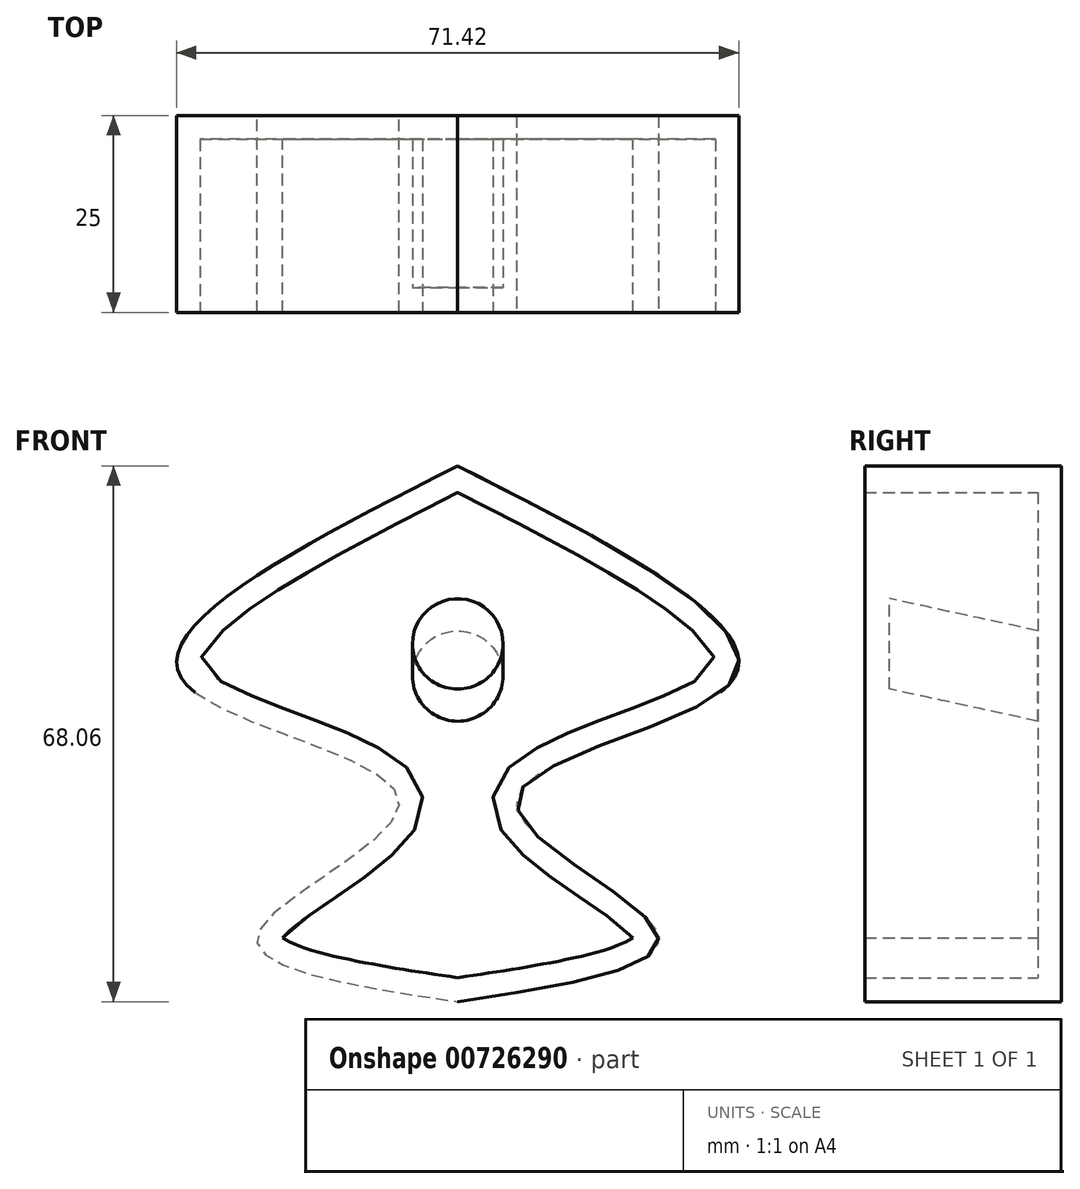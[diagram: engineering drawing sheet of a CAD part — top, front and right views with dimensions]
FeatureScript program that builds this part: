
annotation { "Feature Type Name" : "Feature", "Feature Type Description" : "" }
export const myFeature = defineFeature(function(context is Context, id is Id, definition is map)
    precondition{}
    {
        {
            var Q0;
            Q0=qCreatedBy(makeId("Front.planeOp"),FACE);
            var sketch = newSketch(context, id + "F0", { "sketchPlane" : qUnion([Q0])});
            skFitSpline(sketch, "E0", {"points": [v(0, 27.34) * mm, v(-34.86, 0) * mm, v(-7.47, -15.18) * mm, v(-25.3, -31.87) * mm, v(0, -40.72) * mm], "startDerivative": vector(-202.32, -102.92) * mm, "endDerivative": vector(177.56, -26.56) * mm});
            skFitSpline(sketch, "E1.MirrorCS", {"points": [v(0, 27.34) * mm, v(34.86, 0) * mm, v(7.47, -15.18) * mm, v(25.3, -31.87) * mm, v(0, -40.72) * mm], "startDerivative": vector(202.32, -102.92) * mm, "endDerivative": vector(-177.56, -26.56) * mm});
            skSolve(sketch);
        }
        {
            var Q0;
            Q0 = qSketchRegion(id + "F0", true);
            extrude(context, id + "F1", {"entities" : qUnion([Q0]), "depth" : 25 * mm, "offsetDistance" : 25 * mm});
        }
        {
            var Q0;
            Q0=makeQuery(id+"F1.opExtrude","CAP_FACE",FACE,{"disambiguationData":[OSD([sQuery(id+"F0.wireOp",EDGE,"E0"),sQuery(id+"F0.wireOp",EDGE,"E1.MirrorCS")])],"isStart":false});
            shell(context, id + "F2", {"entities" : qUnion([Q0]), "thickness" : 3 * mm});
        }
        {
            var Q0;
            Q0=qCreatedBy(makeId("Front.planeOp"),FACE);
            var sketch = newSketch(context, id + "F3", { "sketchPlane" : qUnion([Q0])});
            skCircle(sketch, "E2", {"center": v(0, 0) * mm, "radius": 5.75 * mm});
            skSolve(sketch);
        }
        {
            var Q0;
            Q0=qCreatedBy(makeId("Right.planeOp"),FACE);
            var sketch = newSketch(context, id + "F4", { "sketchPlane" : qUnion([Q0])});
            skLineSegment(sketch, "E3", {"start": v(0, -1.42) * mm, "end": v(-21.86, 3.31) * mm});
            skSolve(sketch);
        }
        {
            var Q0;
            Q0 = qSketchRegion(id + "F3", true);
            var Q1;
            Q1 = qConstructionFilter(qBodyType(qCreatedBy(id + "F4" ,EDGE), BodyType.WIRE), ConstructionObject.NO);
            sweep(context, id + "F5", {"operationType" : NewBodyOperationType.ADD, "profiles" : qUnion([Q0]), "path" : qUnion([Q1])});
        }
    });
